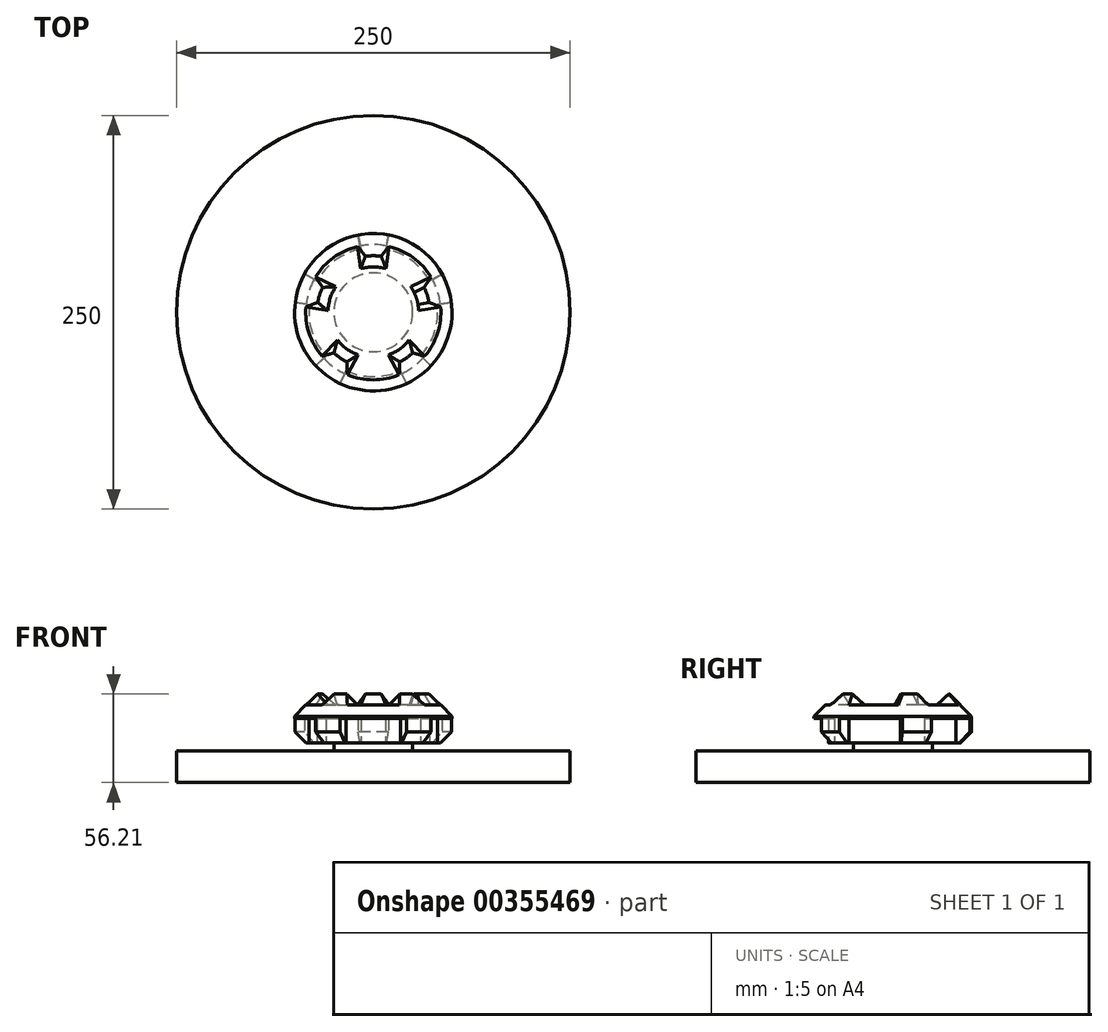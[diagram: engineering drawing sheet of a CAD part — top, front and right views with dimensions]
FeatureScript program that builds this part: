
annotation { "Feature Type Name" : "Feature", "Feature Type Description" : "" }
export const myFeature = defineFeature(function(context is Context, id is Id, definition is map)
    precondition{}
    {
        {
            var Q0;
            Q0=qCreatedBy(makeId("Top.planeOp"),FACE);
            var sketch = newSketch(context, id + "F0", { "sketchPlane" : qUnion([Q0])});
            skCircle(sketch, "E0", {"center": v(0, 0) * mm, "radius": 50 * mm});
            skSolve(sketch);
        }
        {
            var Q0;
            Q0=makeQuery(id+"F0.imprint","IMPRINT",FACE,{"disambiguationData":[TD([[makeQuery(id+"F0.imprint","IMPRINT",EDGE,{"derivedFrom":sQuery(id+"F0.wireOp",EDGE,"E0")}),1.0]])]});
            extrude(context, id + "F1", {"entities" : qUnion([Q0]), "depth" : 14.14 * mm, "hasSecondDirection" : true, "secondDirectionOppositeDirection" : true, "secondDirectionDepth" : 17.07 * mm});
        }
        {
            var Q0;
            Q0=makeQuery(id+"F1.opExtrude","CAP_EDGE",EDGE,{"disambiguationData":[OSD([sQuery(id+"F0.wireOp",EDGE,"E0")])],"isStart":false});
            chamfer(context, id + "F2", {"entities" : qUnion([Q0]), "width" : 14.14 * mm, "tangentPropagation" : true});
        }
        {
            var Q0;
            Q0=makeQuery(id+"F1.opExtrude","CAP_FACE",FACE,{"disambiguationData":[OSD([sQuery(id+"F0.wireOp",EDGE,"E0")])],"isStart":true});
            extrude(context, id + "F3", {"entities" : qUnion([Q0]), "oppositeDirection" : true, "depth" : 50 * mm});
        }
        {
            var Q0;
            Q0=makeQuery(id+"F3.opExtrude","CAP_EDGE",EDGE,{"disambiguationData":[OSD([sQuery(id+"F0.wireOp",EDGE,"E0")])],"isStart":true});
            chamfer(context, id + "F4", {"entities" : qUnion([Q0]), "chamferType" : ChamferType.OFFSET_ANGLE, "width" : 7.07 * mm, "oppositeDirection" : false, "angle" : 30 * degree, "tangentPropagation" : true});
        }
        {
            var Q0;
            Q0=makeQuery(id+"F1.opExtrude","CAP_EDGE",EDGE,{"disambiguationData":[OSD([sQuery(id+"F0.wireOp",EDGE,"E0")])],"isStart":true});
            chamfer(context, id + "F5", {"entities" : qUnion([Q0]), "width" : 7.07 * mm, "tangentPropagation" : true});
        }
        {
            var Q0;
            Q0=makeQuery(id+"F1.opExtrude","CAP_FACE",FACE,{"disambiguationData":[OSD([sQuery(id+"F0.wireOp",EDGE,"E0")])],"isStart":true});
            var sketch = newSketch(context, id + "F6", { "sketchPlane" : qUnion([Q0])});
            skCircle(sketch, "E1", {"center": v(0, 0) * mm, "radius": 25 * mm});
            skSolve(sketch);
        }
        {
            var Q0;
            Q0=makeQuery(id+"F6.imprint","IMPRINT",FACE,{"disambiguationData":[TD([[makeQuery(id+"F6.imprint","IMPRINT",EDGE,{"derivedFrom":sQuery(id+"F6.wireOp",EDGE,"E1")}),1.0]])]});
            extrude(context, id + "F7", {"entities" : qUnion([Q0]), "depth" : 5 * mm});
        }
        {
            var Q0;
            Q0=makeQuery(id+"F7.opExtrude","CAP_FACE",FACE,{"disambiguationData":[OSD([sQuery(id+"F6.wireOp",EDGE,"E1")])],"isStart":false});
            var sketch = newSketch(context, id + "F8", { "sketchPlane" : qUnion([Q0])});
            skCircle(sketch, "E2", {"center": v(0, 0) * mm, "radius": 125 * mm});
            skSolve(sketch);
        }
        {
            var Q0;
            Q0=makeQuery(id+"F8.imprint","IMPRINT",FACE,{"disambiguationData":[TD([[makeQuery(id+"F8.imprint","IMPRINT",EDGE,{"derivedFrom":makeQuery(id+"F7.opExtrude","CAP_EDGE",EDGE,{"disambiguationData":[OSD([sQuery(id+"F6.wireOp",EDGE,"E1")])],"isStart":false})}),1.0]])]});
            var Q1;
            Q1=makeQuery(id+"F8.imprint","IMPRINT",FACE,{"disambiguationData":[TD([[makeQuery(id+"F8.imprint","IMPRINT",EDGE,{"derivedFrom":sQuery(id+"F8.wireOp",EDGE,"E2")}),1.0]])]});
            extrude(context, id + "F9", {"entities" : qUnion([Q0, Q1]), "depth" : 20 * mm});
        }
        {
            var Q0;
            Q0=makeQuery(id+"F1.opExtrude","CAP_FACE",FACE,{"disambiguationData":[OSD([sQuery(id+"F0.wireOp",EDGE,"E0")])],"isStart":false});
            var sketch = newSketch(context, id + "F10", { "sketchPlane" : qUnion([Q0])});
            skCircle(sketch, "E3", {"center": v(0, 0) * mm, "radius": 35.86 * mm, "construction": true});
            skLineSegment(sketch, "E4.bottom", {"start": v(5, 35.5) * mm, "end": v(-5, 35.5) * mm, "construction": true});
            skLineSegment(sketch, "E4.top", {"start": v(5, 74.5) * mm, "end": v(-5, 74.5) * mm, "construction": true});
            skLineSegment(sketch, "E4.left", {"start": v(5, 35.5) * mm, "end": v(5, 74.5) * mm, "construction": true});
            skLineSegment(sketch, "E4.right", {"start": v(-5, 35.5) * mm, "end": v(-5, 74.5) * mm, "construction": true});
            skPoint(sketch, "E4.middle", {"position": v(0, 55) * mm});
            skLineSegment(sketch, "E5.bottom", {"start": v(32.22, 15.73) * mm, "end": v(69.3, 27.77) * mm, "construction": true});
            skLineSegment(sketch, "E5.top", {"start": v(35.31, 6.22) * mm, "end": v(72.4, 18.26) * mm, "construction": true});
            skLineSegment(sketch, "E5.left", {"start": v(32.22, 15.73) * mm, "end": v(35.31, 6.22) * mm, "construction": true});
            skLineSegment(sketch, "E5.right", {"start": v(69.3, 27.77) * mm, "end": v(72.4, 18.26) * mm, "construction": true});
            skPoint(sketch, "E5.middle", {"position": v(52.3, 17) * mm});
            skLineSegment(sketch, "E6.bottom", {"start": v(24.92, -25.79) * mm, "end": v(16.83, -31.67) * mm, "construction": true});
            skLineSegment(sketch, "E6.top", {"start": v(47.83, -57.33) * mm, "end": v(39.74, -63.2) * mm, "construction": true});
            skLineSegment(sketch, "E6.left", {"start": v(24.92, -25.79) * mm, "end": v(47.83, -57.33) * mm, "construction": true});
            skLineSegment(sketch, "E6.right", {"start": v(16.83, -31.67) * mm, "end": v(39.74, -63.2) * mm, "construction": true});
            skPoint(sketch, "E6.middle", {"position": v(32.33, -44.5) * mm});
            skLineSegment(sketch, "E7.bottom", {"start": v(-35.31, 6.22) * mm, "end": v(-72.4, 18.26) * mm, "construction": true});
            skLineSegment(sketch, "E7.top", {"start": v(-32.22, 15.73) * mm, "end": v(-69.3, 27.77) * mm, "construction": true});
            skLineSegment(sketch, "E7.left", {"start": v(-35.31, 6.22) * mm, "end": v(-32.22, 15.73) * mm, "construction": true});
            skLineSegment(sketch, "E7.right", {"start": v(-72.4, 18.26) * mm, "end": v(-69.3, 27.77) * mm, "construction": true});
            skPoint(sketch, "E7.middle", {"position": v(-52.3, 17) * mm});
            skLineSegment(sketch, "E8.bottom", {"start": v(-16.83, -31.67) * mm, "end": v(-24.92, -25.79) * mm, "construction": true});
            skLineSegment(sketch, "E8.top", {"start": v(-39.74, -63.2) * mm, "end": v(-47.83, -57.33) * mm, "construction": true});
            skLineSegment(sketch, "E8.left", {"start": v(-16.83, -31.67) * mm, "end": v(-39.74, -63.2) * mm, "construction": true});
            skLineSegment(sketch, "E8.right", {"start": v(-24.92, -25.79) * mm, "end": v(-47.83, -57.33) * mm, "construction": true});
            skPoint(sketch, "E8.middle", {"position": v(-32.33, -44.5) * mm});
            skCircle(sketch, "E9", {"center": v(0, 0) * mm, "radius": 50 * mm, "construction": true});
            skLineSegment(sketch, "E10", {"start": v(6.97, 49.51) * mm, "end": v(0, 0) * mm, "construction": true});
            skLineSegment(sketch, "E11", {"start": v(44.93, 21.93) * mm, "end": v(0, 0) * mm, "construction": true});
            skLineSegment(sketch, "E12", {"start": v(0, 0) * mm, "end": v(49.24, 8.67) * mm, "construction": true});
            skLineSegment(sketch, "E13", {"start": v(34.74, -35.96) * mm, "end": v(0, 0) * mm, "construction": true});
            skLineSegment(sketch, "E14", {"start": v(23.46, -44.15) * mm, "end": v(0, 0) * mm, "construction": true});
            skLineSegment(sketch, "E15", {"start": v(-23.46, -44.15) * mm, "end": v(0, 0) * mm, "construction": true});
            skLineSegment(sketch, "E16", {"start": v(-34.74, -35.96) * mm, "end": v(0, 0) * mm, "construction": true});
            skLineSegment(sketch, "E17", {"start": v(-49.24, 8.67) * mm, "end": v(0, 0) * mm, "construction": true});
            skLineSegment(sketch, "E18", {"start": v(-44.93, 21.93) * mm, "end": v(0, 0) * mm, "construction": true});
            skLineSegment(sketch, "E19", {"start": v(-6.97, 49.51) * mm, "end": v(0, 0) * mm, "construction": true});
            skArc(sketch, "E20", {"start": v(6.97, 49.51) * mm, "mid": v(29.39, 40.45) * mm, "end": v(44.93, 21.93) * mm});
            skArc(sketch, "E21", {"start": v(49.24, 8.67) * mm, "mid": v(47.55, -15.45) * mm, "end": v(34.74, -35.96) * mm});
            skArc(sketch, "E22", {"start": v(23.46, -44.15) * mm, "mid": v(0, -50) * mm, "end": v(-23.46, -44.15) * mm});
            skArc(sketch, "E23", {"start": v(-34.74, -35.96) * mm, "mid": v(-47.55, -15.45) * mm, "end": v(-49.24, 8.67) * mm});
            skArc(sketch, "E24", {"start": v(-44.93, 21.93) * mm, "mid": v(-29.39, 40.45) * mm, "end": v(-6.97, 49.51) * mm});
            skCircle(sketch, "E25", {"center": v(0, 0) * mm, "radius": 28.79 * mm, "construction": true});
            skLineSegment(sketch, "E26", {"start": v(-6.97, 49.51) * mm, "end": v(-4.01, 28.5) * mm});
            skLineSegment(sketch, "E27", {"start": v(4.01, 28.5) * mm, "end": v(6.97, 49.51) * mm});
            skLineSegment(sketch, "E28", {"start": v(25.87, 12.63) * mm, "end": v(44.93, 21.93) * mm});
            skLineSegment(sketch, "E29", {"start": v(28.35, 5) * mm, "end": v(49.24, 8.67) * mm});
            skLineSegment(sketch, "E30", {"start": v(20, -20.7) * mm, "end": v(34.74, -35.96) * mm});
            skLineSegment(sketch, "E31", {"start": v(13.5, -25.42) * mm, "end": v(23.46, -44.15) * mm});
            skLineSegment(sketch, "E32", {"start": v(-13.5, -25.42) * mm, "end": v(-23.46, -44.15) * mm});
            skLineSegment(sketch, "E33", {"start": v(-20, -20.7) * mm, "end": v(-34.74, -35.96) * mm});
            skLineSegment(sketch, "E34", {"start": v(-28.35, 5) * mm, "end": v(-49.24, 8.67) * mm});
            skLineSegment(sketch, "E35", {"start": v(-25.87, 12.63) * mm, "end": v(-44.93, 21.93) * mm});
            skArc(sketch, "E36", {"start": v(-4.01, 28.5) * mm, "mid": v(0, 28.79) * mm, "end": v(4.01, 28.5) * mm});
            skArc(sketch, "E37", {"start": v(25.87, 12.63) * mm, "mid": v(27.38, 8.9) * mm, "end": v(28.35, 5) * mm});
            skArc(sketch, "E38", {"start": v(20, -20.7) * mm, "mid": v(16.92, -23.29) * mm, "end": v(13.5, -25.42) * mm});
            skArc(sketch, "E39", {"start": v(-13.5, -25.42) * mm, "mid": v(-16.92, -23.29) * mm, "end": v(-20, -20.7) * mm});
            skArc(sketch, "E40", {"start": v(-28.35, 5) * mm, "mid": v(-27.38, 8.9) * mm, "end": v(-25.87, 12.63) * mm});
            skCircle(sketch, "E41.cCircle", {"center": v(0, 0) * mm, "radius": 55 * mm, "construction": true});
            skLineSegment(sketch, "E41.0", {"start": v(32.33, 44.5) * mm, "end": v(52.3, 17) * mm, "construction": true});
            skLineSegment(sketch, "E41.1", {"start": v(52.3, 17) * mm, "end": v(52.3, -17) * mm, "construction": true});
            skLineSegment(sketch, "E41.2", {"start": v(52.3, -17) * mm, "end": v(32.33, -44.5) * mm, "construction": true});
            skLineSegment(sketch, "E41.3", {"start": v(32.33, -44.5) * mm, "end": v(0, -55) * mm, "construction": true});
            skLineSegment(sketch, "E41.4", {"start": v(0, -55) * mm, "end": v(-32.33, -44.5) * mm, "construction": true});
            skLineSegment(sketch, "E41.5", {"start": v(-32.33, -44.5) * mm, "end": v(-52.3, -17) * mm, "construction": true});
            skLineSegment(sketch, "E41.6", {"start": v(-52.3, -17) * mm, "end": v(-52.3, 17) * mm, "construction": true});
            skLineSegment(sketch, "E41.7", {"start": v(-52.3, 17) * mm, "end": v(-32.33, 44.5) * mm, "construction": true});
            skLineSegment(sketch, "E41.8", {"start": v(-32.33, 44.5) * mm, "end": v(0, 55) * mm, "construction": true});
            skLineSegment(sketch, "E41.9", {"start": v(0, 55) * mm, "end": v(32.33, 44.5) * mm, "construction": true});
            skSolve(sketch);
        }
        {
            var Q0;
            Q0=qSketchRegion(id+"F10",true);
            extrude(context, id + "F11", {"entities" : qUnion([Q0]), "operationType" : NewBodyOperationType.REMOVE, "oppositeDirection" : true, "depth" : 7.07 * mm});
        }
        {
            var Q0;
            Q0=makeQuery(id+"F11.boolean.opBoolean","COPY",EDGE,{"derivedFrom":makeQuery(id+"F11.opExtrude","CAP_EDGE",EDGE,{"disambiguationData":[OSD([sQuery(id+"F10.wireOp",EDGE,"E40")])],"isStart":true})});
            var Q1;
            Q1=makeQuery(id+"F11.boolean.opBoolean","COPY",EDGE,{"derivedFrom":makeQuery(id+"F11.opExtrude","CAP_EDGE",EDGE,{"disambiguationData":[OSD([sQuery(id+"F10.wireOp",EDGE,"E36")])],"isStart":true})});
            var Q2;
            Q2=makeQuery(id+"F11.boolean.opBoolean","COPY",EDGE,{"derivedFrom":makeQuery(id+"F11.opExtrude","CAP_EDGE",EDGE,{"disambiguationData":[OSD([sQuery(id+"F10.wireOp",EDGE,"E37")])],"isStart":true})});
            var Q3;
            Q3=makeQuery(id+"F11.boolean.opBoolean","COPY",EDGE,{"derivedFrom":makeQuery(id+"F11.opExtrude","CAP_EDGE",EDGE,{"disambiguationData":[OSD([sQuery(id+"F10.wireOp",EDGE,"E38")])],"isStart":true})});
            var Q4;
            Q4=makeQuery(id+"F11.boolean.opBoolean","COPY",EDGE,{"derivedFrom":makeQuery(id+"F11.opExtrude","CAP_EDGE",EDGE,{"disambiguationData":[OSD([sQuery(id+"F10.wireOp",EDGE,"E39")])],"isStart":true})});
            chamfer(context, id + "F12", {"entities" : qUnion([Q0, Q1, Q2, Q3, Q4]), "width" : 7.07 * mm, "tangentPropagation" : true});
        }
        {
            var Q0;
            Q0=makeQuery(id+"F11.boolean.opBoolean","COPY",EDGE,{"derivedFrom":makeQuery(id+"F11.opExtrude","CAP_EDGE",EDGE,{"disambiguationData":[OSD([sQuery(id+"F10.wireOp",EDGE,"E34")])],"isStart":false})});
            var Q1;
            Q1=makeQuery(id+"F11.boolean.opBoolean","COPY",EDGE,{"derivedFrom":makeQuery(id+"F11.opExtrude","CAP_EDGE",EDGE,{"disambiguationData":[OSD([sQuery(id+"F10.wireOp",EDGE,"E33")])],"isStart":false})});
            var Q2;
            Q2=makeQuery(id+"F11.boolean.opBoolean","COPY",EDGE,{"derivedFrom":makeQuery(id+"F11.opExtrude","CAP_EDGE",EDGE,{"disambiguationData":[OSD([sQuery(id+"F10.wireOp",EDGE,"E32")])],"isStart":false})});
            var Q3;
            Q3=makeQuery(id+"F11.boolean.opBoolean","COPY",EDGE,{"derivedFrom":makeQuery(id+"F11.opExtrude","CAP_EDGE",EDGE,{"disambiguationData":[OSD([sQuery(id+"F10.wireOp",EDGE,"E31")])],"isStart":false})});
            var Q4;
            Q4=makeQuery(id+"F11.boolean.opBoolean","COPY",EDGE,{"derivedFrom":makeQuery(id+"F11.opExtrude","CAP_EDGE",EDGE,{"disambiguationData":[OSD([sQuery(id+"F10.wireOp",EDGE,"E30")])],"isStart":false})});
            var Q5;
            Q5=makeQuery(id+"F11.boolean.opBoolean","COPY",EDGE,{"derivedFrom":makeQuery(id+"F11.opExtrude","CAP_EDGE",EDGE,{"disambiguationData":[OSD([sQuery(id+"F10.wireOp",EDGE,"E29")])],"isStart":false})});
            var Q6;
            Q6=makeQuery(id+"F11.boolean.opBoolean","COPY",EDGE,{"derivedFrom":makeQuery(id+"F11.opExtrude","CAP_EDGE",EDGE,{"disambiguationData":[OSD([sQuery(id+"F10.wireOp",EDGE,"E28")])],"isStart":false})});
            var Q7;
            Q7=makeQuery(id+"F11.boolean.opBoolean","COPY",EDGE,{"derivedFrom":makeQuery(id+"F11.opExtrude","CAP_EDGE",EDGE,{"disambiguationData":[OSD([sQuery(id+"F10.wireOp",EDGE,"E27")])],"isStart":false})});
            var Q8;
            Q8=makeQuery(id+"F11.boolean.opBoolean","COPY",EDGE,{"derivedFrom":makeQuery(id+"F11.opExtrude","CAP_EDGE",EDGE,{"disambiguationData":[OSD([sQuery(id+"F10.wireOp",EDGE,"E26")])],"isStart":false})});
            var Q9;
            Q9=makeQuery(id+"F11.boolean.opBoolean","COPY",EDGE,{"derivedFrom":makeQuery(id+"F11.opExtrude","CAP_EDGE",EDGE,{"disambiguationData":[OSD([sQuery(id+"F10.wireOp",EDGE,"E35")])],"isStart":false})});
            chamfer(context, id + "F13", {"entities" : qUnion([Q0, Q1, Q2, Q3, Q4, Q5, Q6, Q7, Q8, Q9]), "chamferType" : ChamferType.OFFSET_ANGLE, "width" : 7.07 * mm, "oppositeDirection" : true, "angle" : 30 * degree, "tangentPropagation" : true});
        }
        {
            var Q0;
            Q0=makeQuery(id+"F1.opExtrude","CAP_FACE",FACE,{"disambiguationData":[OSD([sQuery(id+"F0.wireOp",EDGE,"E0")])],"isStart":true});
            var sketch = newSketch(context, id + "F14", { "sketchPlane" : qUnion([Q0])});
            skCircle(sketch, "E42", {"center": v(0, 0) * mm, "radius": 47.5 * mm, "construction": true});
            skCircle(sketch, "E43", {"center": v(0, 0) * mm, "radius": 50 * mm, "construction": true});
            skCircle(sketch, "E44.cCircle", {"center": v(0, 0) * mm, "radius": 55 * mm});
            skLineSegment(sketch, "E44.0", {"start": v(32.33, 44.5) * mm, "end": v(52.3, 17) * mm, "construction": true});
            skLineSegment(sketch, "E44.1", {"start": v(52.3, 17) * mm, "end": v(52.3, -17) * mm, "construction": true});
            skLineSegment(sketch, "E44.2", {"start": v(52.3, -17) * mm, "end": v(32.33, -44.5) * mm, "construction": true});
            skLineSegment(sketch, "E44.3", {"start": v(32.33, -44.5) * mm, "end": v(0, -55) * mm, "construction": true});
            skLineSegment(sketch, "E44.4", {"start": v(0, -55) * mm, "end": v(-32.33, -44.5) * mm, "construction": true});
            skLineSegment(sketch, "E44.5", {"start": v(-32.33, -44.5) * mm, "end": v(-52.3, -17) * mm, "construction": true});
            skLineSegment(sketch, "E44.6", {"start": v(-52.3, -17) * mm, "end": v(-52.3, 17) * mm, "construction": true});
            skLineSegment(sketch, "E44.7", {"start": v(-52.3, 17) * mm, "end": v(-32.33, 44.5) * mm, "construction": true});
            skLineSegment(sketch, "E44.8", {"start": v(-32.33, 44.5) * mm, "end": v(0, 55) * mm, "construction": true});
            skLineSegment(sketch, "E44.9", {"start": v(0, 55) * mm, "end": v(32.33, 44.5) * mm, "construction": true});
            skCircle(sketch, "E45", {"center": v(0, 0) * mm, "radius": 40.92 * mm, "construction": true});
            skLineSegment(sketch, "E46.bottom", {"start": v(20, 43.08) * mm, "end": v(-20, 43.08) * mm, "construction": true});
            skLineSegment(sketch, "E46.top", {"start": v(20, 66.92) * mm, "end": v(-20, 66.92) * mm, "construction": true});
            skLineSegment(sketch, "E46.left", {"start": v(20, 43.08) * mm, "end": v(20, 66.92) * mm, "construction": true});
            skLineSegment(sketch, "E46.right", {"start": v(-20, 43.08) * mm, "end": v(-20, 66.92) * mm, "construction": true});
            skPoint(sketch, "E46.middle", {"position": v(0, 55) * mm});
            skLineSegment(sketch, "E47.bottom", {"start": v(47.16, -5.7) * mm, "end": v(69.82, 1.66) * mm, "construction": true});
            skLineSegment(sketch, "E47.top", {"start": v(34.8, 32.33) * mm, "end": v(57.46, 39.7) * mm, "construction": true});
            skLineSegment(sketch, "E47.left", {"start": v(47.16, -5.7) * mm, "end": v(34.8, 32.33) * mm, "construction": true});
            skLineSegment(sketch, "E47.right", {"start": v(69.82, 1.66) * mm, "end": v(57.46, 39.7) * mm, "construction": true});
            skPoint(sketch, "E47.middle", {"position": v(52.3, 17) * mm});
            skLineSegment(sketch, "E48.bottom", {"start": v(9.14, -46.61) * mm, "end": v(41.5, -23.1) * mm, "construction": true});
            skLineSegment(sketch, "E48.top", {"start": v(23.15, -65.9) * mm, "end": v(55.51, -42.38) * mm, "construction": true});
            skLineSegment(sketch, "E48.left", {"start": v(9.14, -46.61) * mm, "end": v(23.15, -65.9) * mm, "construction": true});
            skLineSegment(sketch, "E48.right", {"start": v(41.5, -23.1) * mm, "end": v(55.51, -42.38) * mm, "construction": true});
            skPoint(sketch, "E48.middle", {"position": v(32.33, -44.5) * mm});
            skLineSegment(sketch, "E49.bottom", {"start": v(-9.14, -46.61) * mm, "end": v(-41.5, -23.1) * mm, "construction": true});
            skLineSegment(sketch, "E49.top", {"start": v(-23.15, -65.9) * mm, "end": v(-55.51, -42.38) * mm, "construction": true});
            skLineSegment(sketch, "E49.left", {"start": v(-9.14, -46.61) * mm, "end": v(-23.15, -65.9) * mm, "construction": true});
            skLineSegment(sketch, "E49.right", {"start": v(-41.5, -23.1) * mm, "end": v(-55.51, -42.38) * mm, "construction": true});
            skPoint(sketch, "E49.middle", {"position": v(-32.33, -44.5) * mm});
            skLineSegment(sketch, "E50.bottom", {"start": v(-47.16, -5.7) * mm, "end": v(-69.82, 1.66) * mm, "construction": true});
            skLineSegment(sketch, "E50.top", {"start": v(-34.8, 32.33) * mm, "end": v(-57.46, 39.7) * mm, "construction": true});
            skLineSegment(sketch, "E50.left", {"start": v(-47.16, -5.7) * mm, "end": v(-34.8, 32.33) * mm, "construction": true});
            skLineSegment(sketch, "E50.right", {"start": v(-69.82, 1.66) * mm, "end": v(-57.46, 39.7) * mm, "construction": true});
            skPoint(sketch, "E50.middle", {"position": v(-52.3, 17) * mm});
            skLineSegment(sketch, "E51", {"start": v(21.05, 45.35) * mm, "end": v(0, 0) * mm, "construction": true});
            skLineSegment(sketch, "E52", {"start": v(36.63, 34.04) * mm, "end": v(0, 0) * mm, "construction": true});
            skLineSegment(sketch, "E53", {"start": v(49.64, -6) * mm, "end": v(0, 0) * mm, "construction": true});
            skLineSegment(sketch, "E54", {"start": v(43.69, -24.32) * mm, "end": v(0, 0) * mm, "construction": true});
            skLineSegment(sketch, "E55", {"start": v(9.63, -49.06) * mm, "end": v(0, 0) * mm, "construction": true});
            skLineSegment(sketch, "E56", {"start": v(-9.63, -49.06) * mm, "end": v(0, 0) * mm, "construction": true});
            skLineSegment(sketch, "E57", {"start": v(-43.69, -24.32) * mm, "end": v(0, 0) * mm, "construction": true});
            skLineSegment(sketch, "E58", {"start": v(-49.64, -6) * mm, "end": v(0, 0) * mm, "construction": true});
            skLineSegment(sketch, "E59", {"start": v(-36.63, 34.04) * mm, "end": v(0, 0) * mm, "construction": true});
            skLineSegment(sketch, "E60", {"start": v(-21.05, 45.35) * mm, "end": v(0, 0) * mm, "construction": true});
            skArc(sketch, "E61", {"start": v(21.05, 45.35) * mm, "mid": v(29.39, 40.45) * mm, "end": v(36.63, 34.04) * mm});
            skArc(sketch, "E62", {"start": v(49.64, -6) * mm, "mid": v(47.55, -15.45) * mm, "end": v(43.69, -24.32) * mm});
            skArc(sketch, "E63", {"start": v(9.63, -49.06) * mm, "mid": v(0, -50) * mm, "end": v(-9.63, -49.06) * mm});
            skArc(sketch, "E64", {"start": v(-43.69, -24.32) * mm, "mid": v(-47.55, -15.45) * mm, "end": v(-49.64, -6) * mm});
            skArc(sketch, "E65", {"start": v(-36.63, 34.04) * mm, "mid": v(-29.39, 40.45) * mm, "end": v(-21.05, 45.35) * mm});
            skArc(sketch, "E66", {"start": v(-17.23, 37.11) * mm, "mid": v(0, 40.92) * mm, "end": v(17.23, 37.11) * mm});
            skArc(sketch, "E67", {"start": v(29.97, 27.85) * mm, "mid": v(38.91, 12.64) * mm, "end": v(40.62, -4.92) * mm});
            skArc(sketch, "E68", {"start": v(35.75, -19.9) * mm, "mid": v(24.05, -33.1) * mm, "end": v(7.88, -40.15) * mm});
            skArc(sketch, "E69", {"start": v(-7.88, -40.15) * mm, "mid": v(-24.05, -33.1) * mm, "end": v(-35.75, -19.9) * mm});
            skArc(sketch, "E70", {"start": v(-40.62, -4.92) * mm, "mid": v(-38.91, 12.64) * mm, "end": v(-29.97, 27.85) * mm});
            skLineSegment(sketch, "E71", {"start": v(-36.63, 34.04) * mm, "end": v(-29.97, 27.85) * mm});
            skLineSegment(sketch, "E72", {"start": v(-49.64, -6) * mm, "end": v(-40.62, -4.92) * mm});
            skLineSegment(sketch, "E73", {"start": v(-21.05, 45.35) * mm, "end": v(-17.23, 37.11) * mm});
            skLineSegment(sketch, "E74", {"start": v(21.05, 45.35) * mm, "end": v(17.23, 37.11) * mm});
            skLineSegment(sketch, "E75", {"start": v(36.63, 34.04) * mm, "end": v(29.97, 27.85) * mm});
            skLineSegment(sketch, "E76", {"start": v(49.64, -6) * mm, "end": v(40.62, -4.92) * mm});
            skLineSegment(sketch, "E77", {"start": v(43.69, -24.32) * mm, "end": v(35.75, -19.9) * mm});
            skLineSegment(sketch, "E78", {"start": v(9.63, -49.06) * mm, "end": v(7.88, -40.15) * mm});
            skLineSegment(sketch, "E79", {"start": v(-9.63, -49.06) * mm, "end": v(-7.88, -40.15) * mm});
            skLineSegment(sketch, "E80", {"start": v(-43.69, -24.32) * mm, "end": v(-35.75, -19.9) * mm});
            skSolve(sketch);
        }
        {
            var Q0;
            Q0=qSketchRegion(id+"F14",true);
            var Q1;
            Q1=qConstructionFilter(qBodyType(qCreatedBy(id+"F14",EDGE),BodyType.WIRE),ConstructionObject.NO);
            extrude(context, id + "F15", {"entities" : qUnion([Q0]), "operationType" : NewBodyOperationType.REMOVE, "surfaceEntities" : qUnion([Q1]), "oppositeDirection" : true, "depth" : 15.73 * mm});
        }
        {
            var Q0;
            Q0=makeQuery(id+"F15.boolean.opBoolean","COPY",EDGE,{"disambiguationData":[OD(0.0)],"derivedFrom":makeQuery(id+"F15.opExtrude","CAP_EDGE",EDGE,{"disambiguationData":[OSD([sQuery(id+"F14.wireOp",EDGE,"E70")])],"isStart":false})});
            var Q1;
            Q1=makeQuery(id+"F15.boolean.opBoolean","COPY",EDGE,{"disambiguationData":[OD(0.0)],"derivedFrom":makeQuery(id+"F15.opExtrude","CAP_EDGE",EDGE,{"disambiguationData":[OSD([sQuery(id+"F14.wireOp",EDGE,"E69")])],"isStart":false})});
            var Q2;
            Q2=makeQuery(id+"F15.boolean.opBoolean","COPY",EDGE,{"disambiguationData":[OD(0.0)],"derivedFrom":makeQuery(id+"F15.opExtrude","CAP_EDGE",EDGE,{"disambiguationData":[OSD([sQuery(id+"F14.wireOp",EDGE,"E68")])],"isStart":false})});
            var Q3;
            Q3=makeQuery(id+"F15.boolean.opBoolean","COPY",EDGE,{"disambiguationData":[OD(0.0)],"derivedFrom":makeQuery(id+"F15.opExtrude","CAP_EDGE",EDGE,{"disambiguationData":[OSD([sQuery(id+"F14.wireOp",EDGE,"E67")])],"isStart":false})});
            var Q4;
            Q4=makeQuery(id+"F15.boolean.opBoolean","COPY",EDGE,{"disambiguationData":[OD(0.0)],"derivedFrom":makeQuery(id+"F15.opExtrude","CAP_EDGE",EDGE,{"disambiguationData":[OSD([sQuery(id+"F14.wireOp",EDGE,"E66")])],"isStart":false})});
            chamfer(context, id + "F16", {"entities" : qUnion([Q0, Q1, Q2, Q3, Q4]), "chamferType" : ChamferType.OFFSET_ANGLE, "width" : 15.73 * mm, "oppositeDirection" : true, "angle" : 30 * degree, "tangentPropagation" : true});
        }
        {
            var Q0;
            Q0=makeQuery(id+"F16.opChamfer","BLEND_EDGE",EDGE,{"blendedFrom":[makeQuery(id+"F15.boolean.opBoolean","COPY",EDGE,{"derivedFrom":makeQuery(id+"F15.opExtrude","CAP_EDGE",EDGE,{"disambiguationData":[OSD([sQuery(id+"F14.wireOp",EDGE,"E66")])],"isStart":false})}),makeQuery(id+"F15.boolean.opBoolean","COPY",FACE,{"derivedFrom":makeQuery(id+"F15.opExtrude","SWEPT_FACE",FACE,{"disambiguationData":[OSD([sQuery(id+"F14.wireOp",EDGE,"E73")])]})})],"blendedInto":[makeQuery(id+"F15.boolean.opBoolean","COPY",FACE,{"derivedFrom":makeQuery(id+"F15.opExtrude","SWEPT_FACE",FACE,{"disambiguationData":[OSD([sQuery(id+"F14.wireOp",EDGE,"E73")])]})})]});
            var Q1;
            Q1=makeQuery(id+"F16.opChamfer","BLEND_EDGE",EDGE,{"blendedFrom":[makeQuery(id+"F15.boolean.opBoolean","COPY",EDGE,{"derivedFrom":makeQuery(id+"F15.opExtrude","CAP_EDGE",EDGE,{"disambiguationData":[OSD([sQuery(id+"F14.wireOp",EDGE,"E66")])],"isStart":false})}),makeQuery(id+"F15.boolean.opBoolean","COPY",FACE,{"derivedFrom":makeQuery(id+"F15.opExtrude","SWEPT_FACE",FACE,{"disambiguationData":[OSD([sQuery(id+"F14.wireOp",EDGE,"E74")])]})})],"blendedInto":[makeQuery(id+"F15.boolean.opBoolean","COPY",FACE,{"derivedFrom":makeQuery(id+"F15.opExtrude","SWEPT_FACE",FACE,{"disambiguationData":[OSD([sQuery(id+"F14.wireOp",EDGE,"E74")])]})})]});
            var Q2;
            Q2=makeQuery(id+"F16.opChamfer","BLEND_EDGE",EDGE,{"blendedFrom":[makeQuery(id+"F15.boolean.opBoolean","COPY",EDGE,{"derivedFrom":makeQuery(id+"F15.opExtrude","CAP_EDGE",EDGE,{"disambiguationData":[OSD([sQuery(id+"F14.wireOp",EDGE,"E67")])],"isStart":false})}),makeQuery(id+"F15.boolean.opBoolean","COPY",FACE,{"derivedFrom":makeQuery(id+"F15.opExtrude","SWEPT_FACE",FACE,{"disambiguationData":[OSD([sQuery(id+"F14.wireOp",EDGE,"E75")])]})})],"blendedInto":[makeQuery(id+"F15.boolean.opBoolean","COPY",FACE,{"derivedFrom":makeQuery(id+"F15.opExtrude","SWEPT_FACE",FACE,{"disambiguationData":[OSD([sQuery(id+"F14.wireOp",EDGE,"E75")])]})})]});
            var Q3;
            Q3=makeQuery(id+"F16.opChamfer","BLEND_EDGE",EDGE,{"blendedFrom":[makeQuery(id+"F15.boolean.opBoolean","COPY",EDGE,{"derivedFrom":makeQuery(id+"F15.opExtrude","CAP_EDGE",EDGE,{"disambiguationData":[OSD([sQuery(id+"F14.wireOp",EDGE,"E67")])],"isStart":false})}),makeQuery(id+"F15.boolean.opBoolean","COPY",FACE,{"derivedFrom":makeQuery(id+"F15.opExtrude","SWEPT_FACE",FACE,{"disambiguationData":[OSD([sQuery(id+"F14.wireOp",EDGE,"E76")])]})})],"blendedInto":[makeQuery(id+"F15.boolean.opBoolean","COPY",FACE,{"derivedFrom":makeQuery(id+"F15.opExtrude","SWEPT_FACE",FACE,{"disambiguationData":[OSD([sQuery(id+"F14.wireOp",EDGE,"E76")])]})})]});
            var Q4;
            Q4=makeQuery(id+"F16.opChamfer","BLEND_EDGE",EDGE,{"blendedFrom":[makeQuery(id+"F15.boolean.opBoolean","COPY",EDGE,{"derivedFrom":makeQuery(id+"F15.opExtrude","CAP_EDGE",EDGE,{"disambiguationData":[OSD([sQuery(id+"F14.wireOp",EDGE,"E68")])],"isStart":false})}),makeQuery(id+"F15.boolean.opBoolean","COPY",FACE,{"derivedFrom":makeQuery(id+"F15.opExtrude","SWEPT_FACE",FACE,{"disambiguationData":[OSD([sQuery(id+"F14.wireOp",EDGE,"E77")])]})})],"blendedInto":[makeQuery(id+"F15.boolean.opBoolean","COPY",FACE,{"derivedFrom":makeQuery(id+"F15.opExtrude","SWEPT_FACE",FACE,{"disambiguationData":[OSD([sQuery(id+"F14.wireOp",EDGE,"E77")])]})})]});
            var Q5;
            Q5=makeQuery(id+"F16.opChamfer","BLEND_EDGE",EDGE,{"blendedFrom":[makeQuery(id+"F15.boolean.opBoolean","COPY",EDGE,{"derivedFrom":makeQuery(id+"F15.opExtrude","CAP_EDGE",EDGE,{"disambiguationData":[OSD([sQuery(id+"F14.wireOp",EDGE,"E68")])],"isStart":false})}),makeQuery(id+"F15.boolean.opBoolean","COPY",FACE,{"derivedFrom":makeQuery(id+"F15.opExtrude","SWEPT_FACE",FACE,{"disambiguationData":[OSD([sQuery(id+"F14.wireOp",EDGE,"E78")])]})})],"blendedInto":[makeQuery(id+"F15.boolean.opBoolean","COPY",FACE,{"derivedFrom":makeQuery(id+"F15.opExtrude","SWEPT_FACE",FACE,{"disambiguationData":[OSD([sQuery(id+"F14.wireOp",EDGE,"E78")])]})})]});
            var Q6;
            Q6=makeQuery(id+"F16.opChamfer","BLEND_EDGE",EDGE,{"blendedFrom":[makeQuery(id+"F15.boolean.opBoolean","COPY",EDGE,{"derivedFrom":makeQuery(id+"F15.opExtrude","CAP_EDGE",EDGE,{"disambiguationData":[OSD([sQuery(id+"F14.wireOp",EDGE,"E69")])],"isStart":false})}),makeQuery(id+"F15.boolean.opBoolean","COPY",FACE,{"derivedFrom":makeQuery(id+"F15.opExtrude","SWEPT_FACE",FACE,{"disambiguationData":[OSD([sQuery(id+"F14.wireOp",EDGE,"E79")])]})})],"blendedInto":[makeQuery(id+"F15.boolean.opBoolean","COPY",FACE,{"derivedFrom":makeQuery(id+"F15.opExtrude","SWEPT_FACE",FACE,{"disambiguationData":[OSD([sQuery(id+"F14.wireOp",EDGE,"E79")])]})})]});
            var Q7;
            Q7=makeQuery(id+"F16.opChamfer","BLEND_EDGE",EDGE,{"blendedFrom":[makeQuery(id+"F15.boolean.opBoolean","COPY",EDGE,{"derivedFrom":makeQuery(id+"F15.opExtrude","CAP_EDGE",EDGE,{"disambiguationData":[OSD([sQuery(id+"F14.wireOp",EDGE,"E69")])],"isStart":false})}),makeQuery(id+"F15.boolean.opBoolean","COPY",FACE,{"derivedFrom":makeQuery(id+"F15.opExtrude","SWEPT_FACE",FACE,{"disambiguationData":[OSD([sQuery(id+"F14.wireOp",EDGE,"E80")])]})})],"blendedInto":[makeQuery(id+"F15.boolean.opBoolean","COPY",FACE,{"derivedFrom":makeQuery(id+"F15.opExtrude","SWEPT_FACE",FACE,{"disambiguationData":[OSD([sQuery(id+"F14.wireOp",EDGE,"E80")])]})})]});
            var Q8;
            Q8=makeQuery(id+"F16.opChamfer","BLEND_EDGE",EDGE,{"blendedFrom":[makeQuery(id+"F15.boolean.opBoolean","COPY",EDGE,{"derivedFrom":makeQuery(id+"F15.opExtrude","CAP_EDGE",EDGE,{"disambiguationData":[OSD([sQuery(id+"F14.wireOp",EDGE,"E70")])],"isStart":false})}),makeQuery(id+"F15.boolean.opBoolean","COPY",FACE,{"derivedFrom":makeQuery(id+"F15.opExtrude","SWEPT_FACE",FACE,{"disambiguationData":[OSD([sQuery(id+"F14.wireOp",EDGE,"E72")])]})})],"blendedInto":[makeQuery(id+"F15.boolean.opBoolean","COPY",FACE,{"derivedFrom":makeQuery(id+"F15.opExtrude","SWEPT_FACE",FACE,{"disambiguationData":[OSD([sQuery(id+"F14.wireOp",EDGE,"E72")])]})})]});
            var Q9;
            Q9=makeQuery(id+"F16.opChamfer","BLEND_EDGE",EDGE,{"blendedFrom":[makeQuery(id+"F15.boolean.opBoolean","COPY",EDGE,{"derivedFrom":makeQuery(id+"F15.opExtrude","CAP_EDGE",EDGE,{"disambiguationData":[OSD([sQuery(id+"F14.wireOp",EDGE,"E70")])],"isStart":false})}),makeQuery(id+"F15.boolean.opBoolean","COPY",FACE,{"derivedFrom":makeQuery(id+"F15.opExtrude","SWEPT_FACE",FACE,{"disambiguationData":[OSD([sQuery(id+"F14.wireOp",EDGE,"E71")])]})})],"blendedInto":[makeQuery(id+"F15.boolean.opBoolean","COPY",FACE,{"derivedFrom":makeQuery(id+"F15.opExtrude","SWEPT_FACE",FACE,{"disambiguationData":[OSD([sQuery(id+"F14.wireOp",EDGE,"E71")])]})})]});
            chamfer(context, id + "F17", {"entities" : qUnion([Q0, Q1, Q2, Q3, Q4, Q5, Q6, Q7, Q8, Q9]), "chamferType" : ChamferType.OFFSET_ANGLE, "width" : 5 * mm, "oppositeDirection" : false, "angle" : 60 * degree, "tangentPropagation" : true});
        }
        {
            var Q0;
            Q0=makeQuery(id+"F1.opExtrude","SWEPT_BODY",BODY,{"disambiguationData":[OSD([sQuery(id+"F0.wireOp",EDGE,"E0")])]});
            var Q1;
            Q1=makeQuery(id+"F3.opExtrude","SWEPT_BODY",BODY,{"disambiguationData":[OSD([sQuery(id+"F0.wireOp",EDGE,"E0")])]});
            booleanBodies(context, id + "F18", {"operationType" : BooleanOperationType.INTERSECTION, "tools" : qUnion([Q0, Q1])});
        }
    });
